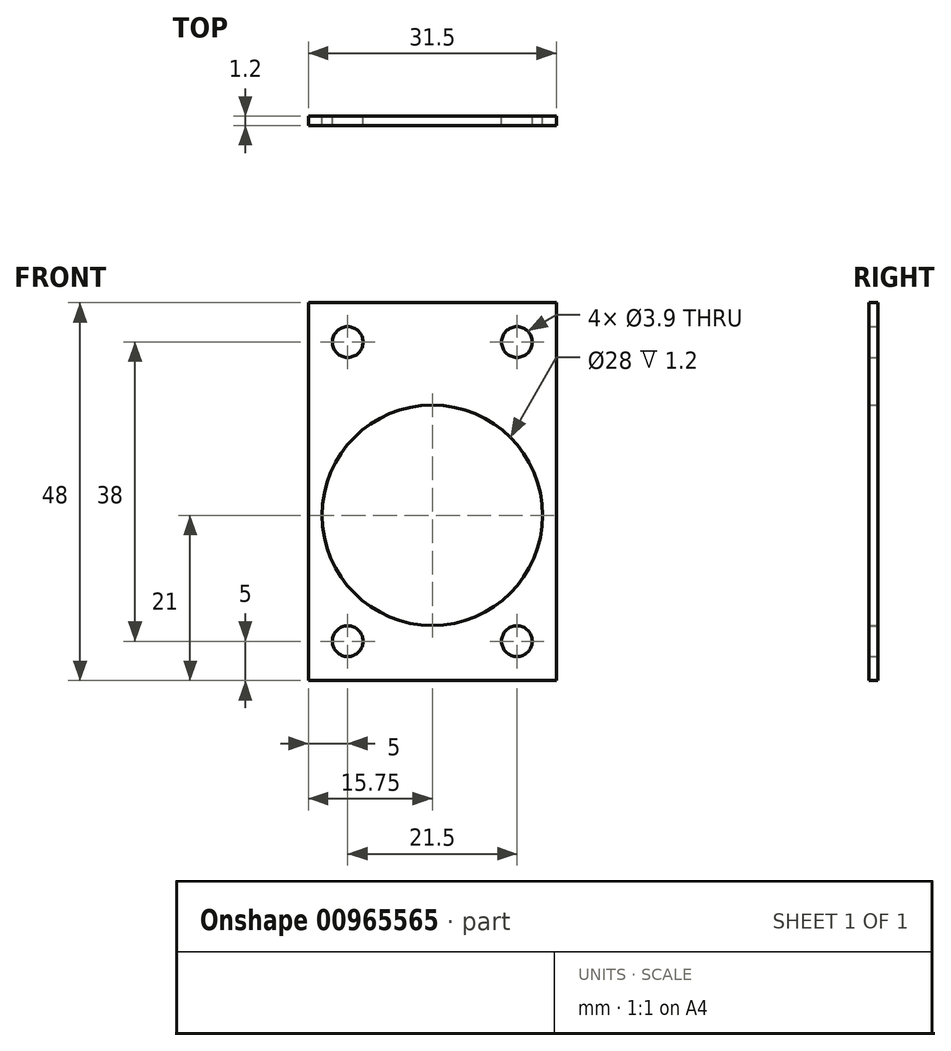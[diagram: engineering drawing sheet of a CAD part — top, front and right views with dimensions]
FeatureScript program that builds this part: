
annotation { "Feature Type Name" : "Feature", "Feature Type Description" : "" }
export const myFeature = defineFeature(function(context is Context, id is Id, definition is map)
    precondition{}
    {
        {
            var Q0;
            Q0=qCreatedBy(makeId("Front.planeOp"),FACE);
            var sketch = newSketch(context, id + "F0", { "sketchPlane" : qUnion([Q0])});
            skLineSegment(sketch, "E0.bottom", {"start": v(-15.75, 25) * mm, "end": v(15.75, 25) * mm});
            skLineSegment(sketch, "E0.top", {"start": v(-15.75, -25) * mm, "end": v(15.75, -25) * mm});
            skLineSegment(sketch, "E0.left", {"start": v(-15.75, 25) * mm, "end": v(-15.75, -25) * mm});
            skLineSegment(sketch, "E0.right", {"start": v(15.75, 25) * mm, "end": v(15.75, -25) * mm});
            skLineSegment(sketch, "E1", {"start": v(15.75, 13.12) * mm, "end": v(0, 13.12) * mm, "construction": true});
            skLineSegment(sketch, "E2", {"start": v(0, -25) * mm, "end": v(0, -4) * mm, "construction": true});
            skCircle(sketch, "E3", {"center": v(0, -4) * mm, "radius": 14 * mm});
            skLineSegment(sketch, "E4.top", {"start": v(-15.75, 23) * mm, "end": v(15.75, 23) * mm});
            skLineSegment(sketch, "E4.left", {"start": v(-15.75, 25) * mm, "end": v(-15.75, 23) * mm});
            skLineSegment(sketch, "E4.right", {"start": v(15.75, 25) * mm, "end": v(15.75, 23) * mm});
            skLineSegment(sketch, "E5.bottom", {"start": v(-15.75, -25) * mm, "end": v(-10.75, -25) * mm, "construction": true});
            skLineSegment(sketch, "E5.top", {"start": v(-15.75, -20) * mm, "end": v(-10.75, -20) * mm, "construction": true});
            skLineSegment(sketch, "E5.left", {"start": v(-15.75, -25) * mm, "end": v(-15.75, -20) * mm, "construction": true});
            skLineSegment(sketch, "E5.right", {"start": v(-10.75, -25) * mm, "end": v(-10.75, -20) * mm, "construction": true});
            skLineSegment(sketch, "E6.bottom", {"start": v(15.75, -25) * mm, "end": v(10.75, -25) * mm, "construction": true});
            skLineSegment(sketch, "E6.top", {"start": v(15.75, -20) * mm, "end": v(10.75, -20) * mm, "construction": true});
            skLineSegment(sketch, "E6.left", {"start": v(15.75, -25) * mm, "end": v(15.75, -20) * mm, "construction": true});
            skLineSegment(sketch, "E6.right", {"start": v(10.75, -25) * mm, "end": v(10.75, -20) * mm, "construction": true});
            skLineSegment(sketch, "E7.bottom", {"start": v(-15.75, 23) * mm, "end": v(-10.75, 23) * mm, "construction": true});
            skLineSegment(sketch, "E7.top", {"start": v(-15.75, 18) * mm, "end": v(-10.75, 18) * mm, "construction": true});
            skLineSegment(sketch, "E7.left", {"start": v(-15.75, 23) * mm, "end": v(-15.75, 18) * mm, "construction": true});
            skLineSegment(sketch, "E7.right", {"start": v(-10.75, 23) * mm, "end": v(-10.75, 18) * mm, "construction": true});
            skLineSegment(sketch, "E8.bottom", {"start": v(15.75, 23) * mm, "end": v(10.75, 23) * mm, "construction": true});
            skLineSegment(sketch, "E8.left", {"start": v(15.75, 23) * mm, "end": v(15.75, 18) * mm, "construction": true});
            skLineSegment(sketch, "E9.top", {"start": v(15.75, 18) * mm, "end": v(10.75, 18) * mm, "construction": true});
            skLineSegment(sketch, "E9.right", {"start": v(10.75, 23) * mm, "end": v(10.75, 18) * mm, "construction": true});
            skCircle(sketch, "E10", {"center": v(-10.75, 18) * mm, "radius": 1.95 * mm});
            skCircle(sketch, "E11", {"center": v(10.75, 18) * mm, "radius": 1.95 * mm});
            skCircle(sketch, "E12", {"center": v(-10.75, -20) * mm, "radius": 1.95 * mm});
            skCircle(sketch, "E13", {"center": v(10.75, -20) * mm, "radius": 1.95 * mm});
            skSolve(sketch);
        }
        {
            var Q0;
            Q0=makeQuery(id+"F0.imprint","IMPRINT",FACE,{"disambiguationData":[TD([[makeQuery(id+"F0.imprint","IMPRINT",EDGE,{"derivedFrom":sQuery(id+"F0.wireOp",EDGE,"E0.top")}),1.0]])]});
            extrude(context, id + "F1", {"entities" : qUnion([Q0]), "depth" : 1.2 * mm, "offsetDistance" : 25 * mm});
        }
    });
